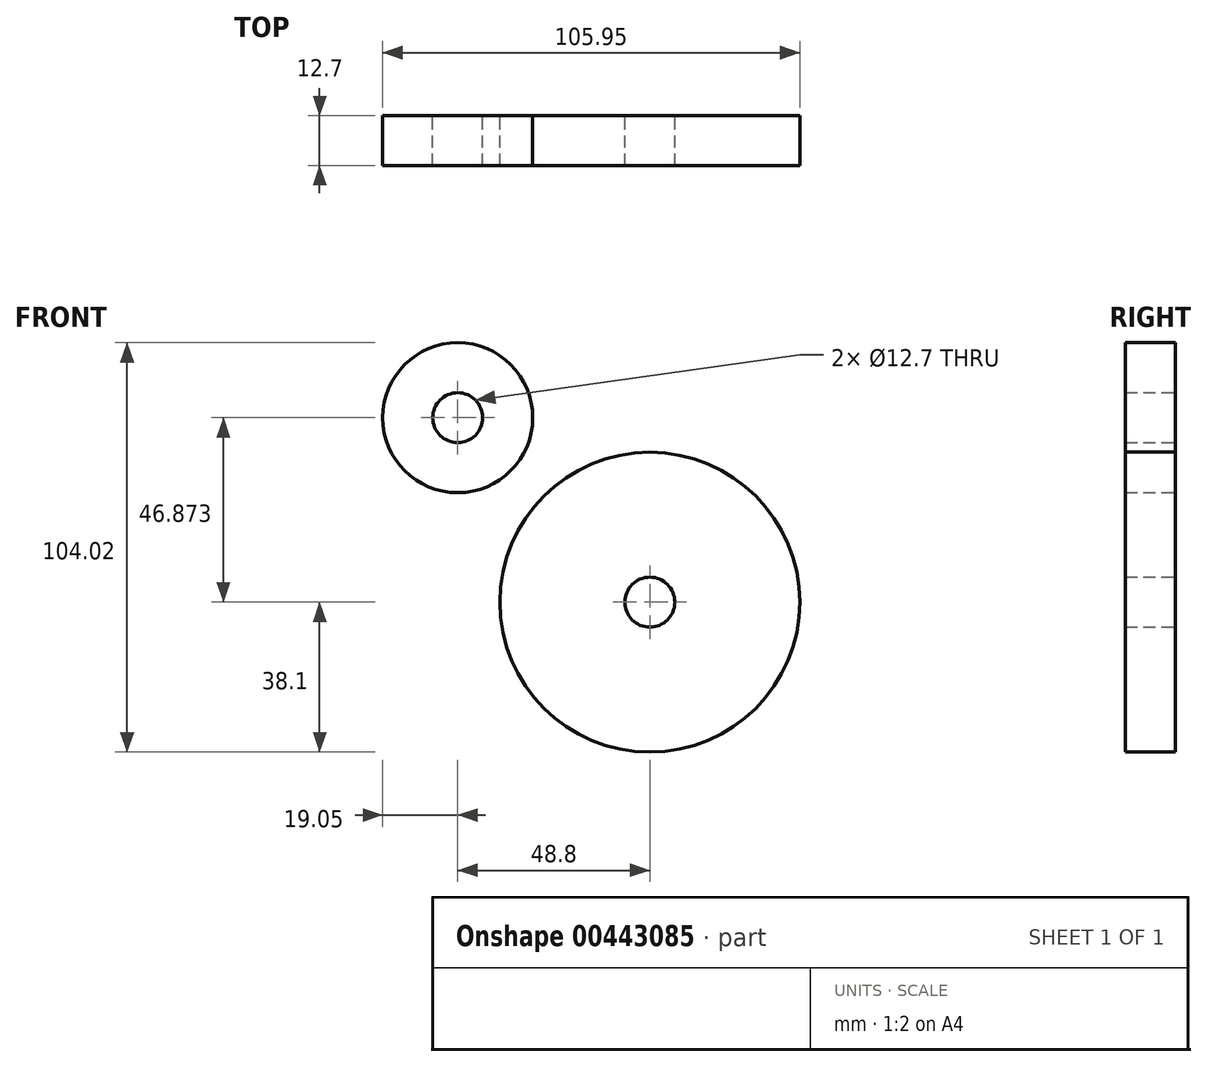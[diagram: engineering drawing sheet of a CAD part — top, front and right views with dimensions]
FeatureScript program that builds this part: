
annotation { "Feature Type Name" : "Feature", "Feature Type Description" : "" }
export const myFeature = defineFeature(function(context is Context, id is Id, definition is map)
    precondition{}
    {
        {
            var Q0;
            Q0=qCreatedBy(makeId("Front.planeOp"),FACE);
            var sketch = newSketch(context, id + "F0", { "sketchPlane" : qUnion([Q0])});
            skCircle(sketch, "E0", {"center": v(0, 0) * mm, "radius": 38.1 * mm});
            skCircle(sketch, "E1", {"center": v(0, 0) * mm, "radius": 6.35 * mm});
            skCircle(sketch, "E2", {"center": v(-48.8, 46.87) * mm, "radius": 19.05 * mm});
            skCircle(sketch, "E3", {"center": v(-48.8, 46.87) * mm, "radius": 6.35 * mm});
            skSolve(sketch);
        }
        {
            var Q0;
            Q0=qSketchRegion(id+"F0",true);
            extrude(context, id + "F1", {"entities" : qUnion([Q0]), "depth" : 12.7 * mm});
        }
    });
